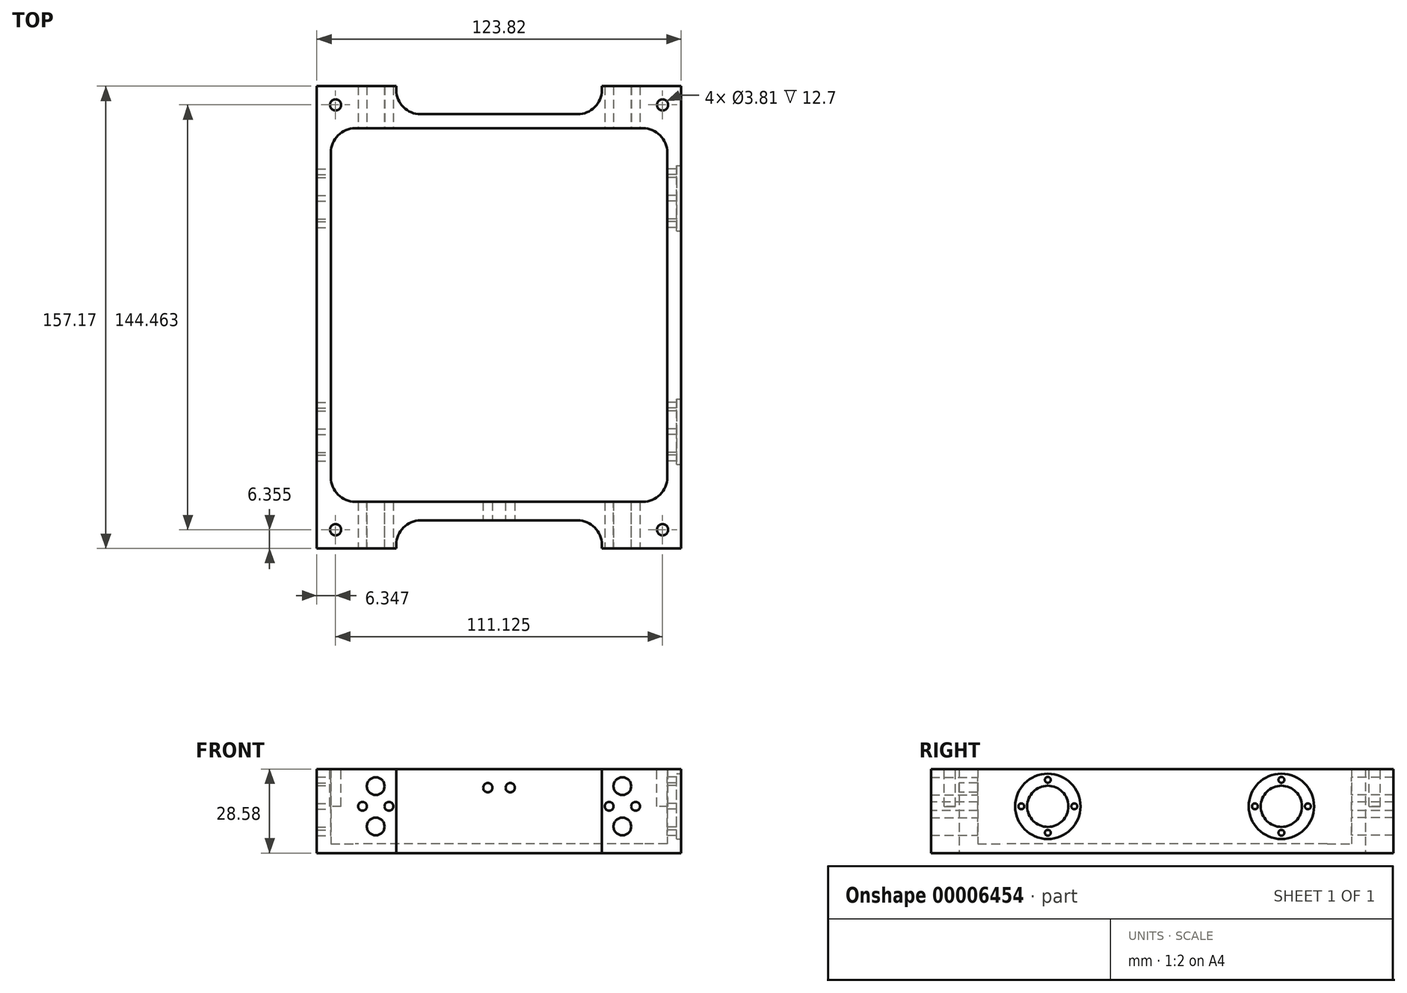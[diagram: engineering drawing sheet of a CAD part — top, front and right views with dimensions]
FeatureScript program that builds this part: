
annotation { "Feature Type Name" : "Feature", "Feature Type Description" : "" }
export const myFeature = defineFeature(function(context is Context, id is Id, definition is map)
    precondition{}
    {
        {
            var Q0;
            Q0=qCreatedBy(makeId("Top.planeOp"),FACE);
            var sketch = newSketch(context, id + "F0", { "sketchPlane" : qUnion([Q0])});
            skLineSegment(sketch, "E0.rect.bottom", {"start": v(48.9, 63.5) * mm, "end": v(-48.9, 63.5) * mm});
            skLineSegment(sketch, "E0.rect.top", {"start": v(48.9, -63.5) * mm, "end": v(-48.9, -63.5) * mm});
            skLineSegment(sketch, "E0.rect.left", {"start": v(57.15, 55.25) * mm, "end": v(57.15, -55.24) * mm});
            skLineSegment(sketch, "E0.rect.right", {"start": v(-57.15, 55.25) * mm, "end": v(-57.15, -55.24) * mm});
            skPoint(sketch, "E0.rect.middle", {"position": v(0, 0) * mm});
            skLineSegment(sketch, "E1.rect.bottom", {"start": v(26.67, 68.26) * mm, "end": v(-26.67, 68.26) * mm});
            skLineSegment(sketch, "E1.rect.top", {"start": v(26.67, -69.85) * mm, "end": v(-26.67, -69.85) * mm});
            skLineSegment(sketch, "E2.top", {"start": v(-61.91, 77.79) * mm, "end": v(-34.93, 77.79) * mm});
            skLineSegment(sketch, "E2.right", {"start": v(-34.93, 76.52) * mm, "end": v(-34.93, 77.79) * mm});
            skLineSegment(sketch, "E3.top", {"start": v(61.91, 77.79) * mm, "end": v(34.92, 77.79) * mm});
            skLineSegment(sketch, "E3.right", {"start": v(34.92, 76.52) * mm, "end": v(34.92, 77.79) * mm});
            skLineSegment(sketch, "E4.top", {"start": v(61.91, -79.37) * mm, "end": v(34.93, -79.37) * mm});
            skLineSegment(sketch, "E4.right", {"start": v(34.93, -78.1) * mm, "end": v(34.93, -79.37) * mm});
            skLineSegment(sketch, "E5.top", {"start": v(-61.91, -79.37) * mm, "end": v(-34.92, -79.37) * mm});
            skLineSegment(sketch, "E5.right", {"start": v(-34.92, -78.1) * mm, "end": v(-34.92, -79.37) * mm});
            skLineSegment(sketch, "E6", {"start": v(-61.91, 77.79) * mm, "end": v(-61.91, -79.37) * mm});
            skLineSegment(sketch, "E7", {"start": v(61.91, -79.37) * mm, "end": v(61.91, 77.79) * mm});
            skLineSegment(sketch, "E8.bottom", {"start": v(-68.26, 71.44) * mm, "end": v(-84.14, 71.44) * mm, "construction": true});
            skLineSegment(sketch, "E8.top", {"start": v(-68.26, 7.94) * mm, "end": v(-84.14, 7.94) * mm, "construction": true});
            skLineSegment(sketch, "E8.left", {"start": v(-68.26, 71.44) * mm, "end": v(-68.26, 7.94) * mm, "construction": true});
            skLineSegment(sketch, "E8.right", {"start": v(-84.14, 71.44) * mm, "end": v(-84.14, 7.94) * mm, "construction": true});
            skLineSegment(sketch, "E9.bottom", {"start": v(-68.26, -71.44) * mm, "end": v(-84.14, -71.44) * mm, "construction": true});
            skLineSegment(sketch, "E9.top", {"start": v(-68.26, -7.94) * mm, "end": v(-84.14, -7.94) * mm, "construction": true});
            skLineSegment(sketch, "E9.left", {"start": v(-68.26, -71.44) * mm, "end": v(-68.26, -7.94) * mm, "construction": true});
            skLineSegment(sketch, "E9.right", {"start": v(-84.14, -71.44) * mm, "end": v(-84.14, -7.94) * mm, "construction": true});
            skLineSegment(sketch, "E10.bottom", {"start": v(87.8, -7) * mm, "end": v(113.59, -7) * mm, "construction": true});
            skLineSegment(sketch, "E10.top", {"start": v(87.8, -69.35) * mm, "end": v(113.59, -69.35) * mm, "construction": true});
            skLineSegment(sketch, "E10.left", {"start": v(87.8, -7) * mm, "end": v(87.8, -69.35) * mm, "construction": true});
            skLineSegment(sketch, "E10.right", {"start": v(113.59, -7) * mm, "end": v(113.59, -69.35) * mm, "construction": true});
            skLineSegment(sketch, "E11.bottom", {"start": v(87.35, 69.72) * mm, "end": v(104.84, 69.72) * mm, "construction": true});
            skLineSegment(sketch, "E11.top", {"start": v(87.35, 26.43) * mm, "end": v(104.84, 26.43) * mm, "construction": true});
            skLineSegment(sketch, "E11.left", {"start": v(87.35, 69.72) * mm, "end": v(87.35, 26.43) * mm, "construction": true});
            skLineSegment(sketch, "E11.right", {"start": v(104.84, 69.72) * mm, "end": v(104.84, 26.43) * mm, "construction": true});
            skLineSegment(sketch, "E12", {"start": v(0, 0) * mm, "end": v(-84.14, 0) * mm, "construction": true});
            skLineSegment(sketch, "E13", {"start": v(-84.14, 7.94) * mm, "end": v(-84.14, 0) * mm, "construction": true});
            skLineSegment(sketch, "E14", {"start": v(-84.14, 0) * mm, "end": v(-84.14, -7.94) * mm, "construction": true});
            skPoint(sketch, "E15.visualSharp", {"position": v(-57.15, 63.5) * mm});
            skArc(sketch, "E15.filletArc", {"start": v(-48.9, 63.5) * mm, "mid": v(-54.73, 61.08) * mm, "end": v(-57.15, 55.25) * mm});
            skPoint(sketch, "E16.visualSharp", {"position": v(57.15, 63.5) * mm});
            skArc(sketch, "E16.filletArc", {"start": v(57.15, 55.25) * mm, "mid": v(54.73, 61.08) * mm, "end": v(48.9, 63.5) * mm});
            skPoint(sketch, "E17.visualSharp", {"position": v(57.15, -63.5) * mm});
            skArc(sketch, "E17.filletArc", {"start": v(48.9, -63.5) * mm, "mid": v(54.73, -61.08) * mm, "end": v(57.15, -55.24) * mm});
            skPoint(sketch, "E18.visualSharp", {"position": v(-57.15, -63.5) * mm});
            skArc(sketch, "E18.filletArc", {"start": v(-57.15, -55.24) * mm, "mid": v(-54.73, -61.08) * mm, "end": v(-48.9, -63.5) * mm});
            skPoint(sketch, "E19.visualSharp", {"position": v(-34.93, 68.26) * mm});
            skArc(sketch, "E19.filletArc", {"start": v(-34.93, 76.52) * mm, "mid": v(-32.5, 70.68) * mm, "end": v(-26.67, 68.26) * mm});
            skPoint(sketch, "E20.visualSharp", {"position": v(34.92, 68.26) * mm});
            skArc(sketch, "E20.filletArc", {"start": v(26.67, 68.26) * mm, "mid": v(32.5, 70.68) * mm, "end": v(34.92, 76.52) * mm});
            skPoint(sketch, "E21.visualSharp", {"position": v(34.93, -69.85) * mm});
            skArc(sketch, "E21.filletArc", {"start": v(34.93, -78.1) * mm, "mid": v(32.5, -72.27) * mm, "end": v(26.67, -69.85) * mm});
            skPoint(sketch, "E22.visualSharp", {"position": v(-34.92, -69.85) * mm});
            skArc(sketch, "E22.filletArc", {"start": v(-26.67, -69.85) * mm, "mid": v(-32.5, -72.27) * mm, "end": v(-34.92, -78.1) * mm});
            skLineSegment(sketch, "E23", {"start": v(-68.26, 39.69) * mm, "end": v(-68.26, -39.69) * mm, "construction": true});
            skSolve(sketch);
        }
        {
            var Q0;
            Q0 = qSketchRegion(id + "F0", true);
            extrude(context, id + "F1", {"entities" : qUnion([Q0]), "depth" : 25.4 * mm});
        }
        {
            var Q0;
            Q0=makeQuery(id+"F1.opExtrude","CAP_FACE",FACE,{"disambiguationData":[OSD([sQuery(id+"F0.wireOp",EDGE,"E0.rect.bottom"),sQuery(id+"F0.wireOp",EDGE,"E0.rect.top"),sQuery(id+"F0.wireOp",EDGE,"E0.rect.left"),sQuery(id+"F0.wireOp",EDGE,"E0.rect.right"),sQuery(id+"F0.wireOp",EDGE,"E1.rect.bottom"),sQuery(id+"F0.wireOp",EDGE,"E1.rect.top"),sQuery(id+"F0.wireOp",EDGE,"E2.top"),sQuery(id+"F0.wireOp",EDGE,"E2.right"),sQuery(id+"F0.wireOp",EDGE,"E3.top"),sQuery(id+"F0.wireOp",EDGE,"E3.right"),sQuery(id+"F0.wireOp",EDGE,"E4.top"),sQuery(id+"F0.wireOp",EDGE,"E4.right"),sQuery(id+"F0.wireOp",EDGE,"E5.top"),sQuery(id+"F0.wireOp",EDGE,"E5.right"),sQuery(id+"F0.wireOp",EDGE,"E6"),sQuery(id+"F0.wireOp",EDGE,"E7"),sQuery(id+"F0.wireOp",EDGE,"E15.filletArc"),sQuery(id+"F0.wireOp",EDGE,"E16.filletArc"),sQuery(id+"F0.wireOp",EDGE,"E17.filletArc"),sQuery(id+"F0.wireOp",EDGE,"E18.filletArc"),sQuery(id+"F0.wireOp",EDGE,"E19.filletArc"),sQuery(id+"F0.wireOp",EDGE,"E20.filletArc"),sQuery(id+"F0.wireOp",EDGE,"E21.filletArc"),sQuery(id+"F0.wireOp",EDGE,"E22.filletArc")])],"isStart":true});
            var sketch = newSketch(context, id + "F2", { "sketchPlane" : qUnion([Q0])});
            skLineSegment(sketch, "E24", {"start": v(-61.91, 79.37) * mm, "end": v(-61.91, -77.79) * mm});
            skLineSegment(sketch, "E25", {"start": v(-61.91, -77.79) * mm, "end": v(-34.93, -77.79) * mm});
            skLineSegment(sketch, "E26", {"start": v(-34.93, -77.79) * mm, "end": v(-34.93, -76.52) * mm});
            skLineSegment(sketch, "E27", {"start": v(34.93, -76.52) * mm, "end": v(34.93, -77.79) * mm});
            skLineSegment(sketch, "E28", {"start": v(34.92, -77.79) * mm, "end": v(61.91, -77.79) * mm});
            skLineSegment(sketch, "E29", {"start": v(61.91, -77.79) * mm, "end": v(61.91, 79.37) * mm});
            skLineSegment(sketch, "E30", {"start": v(61.91, 79.37) * mm, "end": v(34.93, 79.37) * mm});
            skLineSegment(sketch, "E31", {"start": v(34.93, 79.37) * mm, "end": v(34.93, 78.1) * mm});
            skLineSegment(sketch, "E32", {"start": v(26.67, 69.85) * mm, "end": v(-26.67, 69.85) * mm});
            skLineSegment(sketch, "E33", {"start": v(-34.93, 78.1) * mm, "end": v(-34.93, 79.37) * mm});
            skLineSegment(sketch, "E34", {"start": v(-34.92, 79.37) * mm, "end": v(-61.91, 79.37) * mm});
            skLineSegment(sketch, "E35", {"start": v(-26.67, -68.26) * mm, "end": v(26.67, -68.26) * mm});
            skArc(sketch, "E36", {"start": v(-26.67, -68.26) * mm, "mid": v(-32.5, -70.68) * mm, "end": v(-34.92, -76.52) * mm});
            skArc(sketch, "E37", {"start": v(26.67, 69.85) * mm, "mid": v(32.5, 72.27) * mm, "end": v(34.93, 78.1) * mm});
            skArc(sketch, "E38", {"start": v(-34.92, 78.1) * mm, "mid": v(-32.5, 72.27) * mm, "end": v(-26.67, 69.85) * mm});
            skArc(sketch, "E39", {"start": v(34.92, -76.52) * mm, "mid": v(32.5, -70.68) * mm, "end": v(26.67, -68.26) * mm});
            skSolve(sketch);
        }
        {
            var Q0;
            Q0 = qSketchRegion(id + "F2", true);
            extrude(context, id + "F3", {"entities" : qUnion([Q0]), "operationType" : NewBodyOperationType.ADD, "depth" : 3.17 * mm});
        }
        {
            var Q0;
            Q0=makeQuery(id+"F1.opExtrude","SWEPT_FACE",FACE,{"disambiguationData":[OSD([sQuery(id+"F0.wireOp",EDGE,"E0.rect.right")])]});
            var sketch = newSketch(context, id + "F4", { "sketchPlane" : qUnion([Q0])});
            skCircle(sketch, "E40", {"center": v(-39.69, 12.7) * mm, "radius": 7 * mm});
            skCircle(sketch, "E41", {"center": v(39.69, 12.7) * mm, "radius": 7 * mm});
            skCircle(sketch, "E42", {"center": v(-39.69, 12.7) * mm, "radius": 9 * mm, "construction": true});
            skCircle(sketch, "E43", {"center": v(39.69, 12.7) * mm, "radius": 9 * mm, "construction": true});
            skCircle(sketch, "E44", {"center": v(-39.69, 21.7) * mm, "radius": 1 * mm});
            skCircle(sketch, "E45", {"center": v(-30.69, 12.7) * mm, "radius": 1 * mm});
            skCircle(sketch, "E46", {"center": v(-39.69, 3.7) * mm, "radius": 1 * mm});
            skCircle(sketch, "E47", {"center": v(-48.69, 12.7) * mm, "radius": 1 * mm});
            skCircle(sketch, "E48", {"center": v(30.69, 12.7) * mm, "radius": 1 * mm});
            skCircle(sketch, "E49", {"center": v(39.69, 21.7) * mm, "radius": 1 * mm});
            skCircle(sketch, "E50", {"center": v(48.69, 12.7) * mm, "radius": 1 * mm});
            skCircle(sketch, "E51", {"center": v(39.69, 3.7) * mm, "radius": 1 * mm});
            skLineSegment(sketch, "E52", {"start": v(-39.69, 12.7) * mm, "end": v(0, 25.4) * mm, "construction": true});
            skLineSegment(sketch, "E53", {"start": v(0, 25.4) * mm, "end": v(39.69, 12.7) * mm, "construction": true});
            skLineSegment(sketch, "E54", {"start": v(-39.69, 12.7) * mm, "end": v(-39.69, 25.4) * mm, "construction": true});
            skLineSegment(sketch, "E55", {"start": v(-39.69, 12.7) * mm, "end": v(-39.69, 0) * mm, "construction": true});
            skSolve(sketch);
        }
        {
            var Q0;
            Q0 = qSketchRegion(id + "F4", true);
            extrude(context, id + "F5", {"entities" : qUnion([Q0]), "operationType" : NewBodyOperationType.REMOVE, "endBound" : BoundingType.THROUGH_ALL, "oppositeDirection" : true, "depth" : 25.4 * mm});
        }
        {
            var Q0;
            Q0 = qSketchRegion(id + "F4", true);
            extrude(context, id + "F6", {"entities" : qUnion([Q0]), "operationType" : NewBodyOperationType.REMOVE, "endBound" : BoundingType.THROUGH_ALL, "depth" : 25.4 * mm});
        }
        {
            var Q0;
            Q0=makeQuery(id+"F1.opExtrude","CAP_FACE",FACE,{"disambiguationData":[OSD([sQuery(id+"F0.wireOp",EDGE,"E0.rect.bottom"),sQuery(id+"F0.wireOp",EDGE,"E0.rect.top"),sQuery(id+"F0.wireOp",EDGE,"E0.rect.left"),sQuery(id+"F0.wireOp",EDGE,"E0.rect.right"),sQuery(id+"F0.wireOp",EDGE,"E1.rect.bottom"),sQuery(id+"F0.wireOp",EDGE,"E1.rect.top"),sQuery(id+"F0.wireOp",EDGE,"E2.top"),sQuery(id+"F0.wireOp",EDGE,"E2.right"),sQuery(id+"F0.wireOp",EDGE,"E3.top"),sQuery(id+"F0.wireOp",EDGE,"E3.right"),sQuery(id+"F0.wireOp",EDGE,"E4.top"),sQuery(id+"F0.wireOp",EDGE,"E4.right"),sQuery(id+"F0.wireOp",EDGE,"E5.top"),sQuery(id+"F0.wireOp",EDGE,"E5.right"),sQuery(id+"F0.wireOp",EDGE,"E6"),sQuery(id+"F0.wireOp",EDGE,"E7"),sQuery(id+"F0.wireOp",EDGE,"E15.filletArc"),sQuery(id+"F0.wireOp",EDGE,"E16.filletArc"),sQuery(id+"F0.wireOp",EDGE,"E17.filletArc"),sQuery(id+"F0.wireOp",EDGE,"E18.filletArc"),sQuery(id+"F0.wireOp",EDGE,"E19.filletArc"),sQuery(id+"F0.wireOp",EDGE,"E20.filletArc"),sQuery(id+"F0.wireOp",EDGE,"E21.filletArc"),sQuery(id+"F0.wireOp",EDGE,"E22.filletArc")])],"isStart":false});
            var sketch = newSketch(context, id + "F7", { "sketchPlane" : qUnion([Q0])});
            skLineSegment(sketch, "E56.bottom", {"start": v(-55.56, 71.44) * mm, "end": v(55.56, 71.44) * mm, "construction": true});
            skLineSegment(sketch, "E56.top", {"start": v(-55.56, -73.02) * mm, "end": v(55.56, -73.02) * mm, "construction": true});
            skLineSegment(sketch, "E56.left", {"start": v(-55.56, 71.44) * mm, "end": v(-55.56, -73.02) * mm, "construction": true});
            skLineSegment(sketch, "E56.right", {"start": v(55.56, 71.44) * mm, "end": v(55.56, -73.02) * mm, "construction": true});
            skCircle(sketch, "E57", {"center": v(-55.56, 71.44) * mm, "radius": 1.9 * mm});
            skCircle(sketch, "E58", {"center": v(55.56, 71.44) * mm, "radius": 1.9 * mm});
            skCircle(sketch, "E59", {"center": v(55.56, -73.02) * mm, "radius": 1.9 * mm});
            skCircle(sketch, "E60", {"center": v(-55.56, -73.02) * mm, "radius": 1.9 * mm});
            skSolve(sketch);
        }
        {
            var Q0;
            Q0 = qSketchRegion(id + "F7", true);
            extrude(context, id + "F8", {"entities" : qUnion([Q0]), "operationType" : NewBodyOperationType.REMOVE, "oppositeDirection" : true, "depth" : 12.7 * mm});
        }
        {
            var Q0;
            Q0=makeQuery(id+"F3.boolean.opBoolean","MERGE",FACE,{"derivedFrom":[makeQuery(id+"F1.opExtrude","SWEPT_FACE",FACE,{"disambiguationData":[OSD([sQuery(id+"F0.wireOp",EDGE,"E1.rect.top")])]}),makeQuery(id+"F3.opExtrude","SWEPT_FACE",FACE,{"disambiguationData":[OSD([sQuery(id+"F2.wireOp",EDGE,"E32")])]})]});
            var sketch = newSketch(context, id + "F9", { "sketchPlane" : qUnion([Q0])});
            skLineSegment(sketch, "E61.bottom", {"start": v(-6.35, 25.4) * mm, "end": v(6.35, 25.4) * mm, "construction": true});
            skLineSegment(sketch, "E61.top", {"start": v(-6.35, 12.7) * mm, "end": v(6.35, 12.7) * mm, "construction": true});
            skLineSegment(sketch, "E61.left", {"start": v(-6.35, 25.4) * mm, "end": v(-6.35, 12.7) * mm, "construction": true});
            skLineSegment(sketch, "E61.right", {"start": v(6.35, 25.4) * mm, "end": v(6.35, 12.7) * mm, "construction": true});
            skLineSegment(sketch, "E62", {"start": v(-6.35, 25.4) * mm, "end": v(-26.67, 25.4) * mm, "construction": true});
            skLineSegment(sketch, "E63", {"start": v(-26.67, 25.4) * mm, "end": v(-6.35, 25.4) * mm, "construction": true});
            skLineSegment(sketch, "E64", {"start": v(6.35, 25.4) * mm, "end": v(26.67, 25.4) * mm, "construction": true});
            skLineSegment(sketch, "E65", {"start": v(-6.35, 12.7) * mm, "end": v(-26.67, 25.4) * mm, "construction": true});
            skLineSegment(sketch, "E66", {"start": v(6.35, 12.7) * mm, "end": v(26.67, 25.4) * mm, "construction": true});
            skLineSegment(sketch, "E67", {"start": v(-6.35, 19.05) * mm, "end": v(-3.8, 19.05) * mm, "construction": true});
            skLineSegment(sketch, "E68", {"start": v(0, 25.4) * mm, "end": v(4.67, 25.4) * mm, "construction": true});
            skLineSegment(sketch, "E69", {"start": v(6.35, 19.05) * mm, "end": v(3.81, 19.05) * mm, "construction": true});
            skCircle(sketch, "E70", {"center": v(-3.8, 19.05) * mm, "radius": 1.59 * mm});
            skCircle(sketch, "E71", {"center": v(3.81, 19.05) * mm, "radius": 1.59 * mm});
            skSolve(sketch);
        }
        {
            var Q0;
            Q0 = qSketchRegion(id + "F9", true);
            extrude(context, id + "F10", {"entities" : qUnion([Q0]), "operationType" : NewBodyOperationType.REMOVE, "endBound" : BoundingType.UP_TO_NEXT, "oppositeDirection" : true, "depth" : 25.4 * mm});
        }
        {
            var Q0;
            Q0=makeQuery(id+"F1.opExtrude","SWEPT_FACE",FACE,{"disambiguationData":[OSD([sQuery(id+"F0.wireOp",EDGE,"E0.rect.bottom")])]});
            var sketch = newSketch(context, id + "F11", { "sketchPlane" : qUnion([Q0])});
            skCircle(sketch, "E72", {"center": v(-41.91, 19.56) * mm, "radius": 3 * mm});
            skCircle(sketch, "E73", {"center": v(-41.91, 5.84) * mm, "radius": 3 * mm});
            skCircle(sketch, "E74", {"center": v(41.91, 19.56) * mm, "radius": 3 * mm});
            skCircle(sketch, "E75", {"center": v(41.91, 5.84) * mm, "radius": 3 * mm});
            skLineSegment(sketch, "E76.bottom", {"start": v(-41.91, 19.56) * mm, "end": v(41.91, 19.56) * mm, "construction": true});
            skLineSegment(sketch, "E76.top", {"start": v(-41.91, 5.84) * mm, "end": v(41.91, 5.84) * mm, "construction": true});
            skLineSegment(sketch, "E76.left", {"start": v(-41.91, 19.56) * mm, "end": v(-41.91, 5.84) * mm, "construction": true});
            skLineSegment(sketch, "E76.right", {"start": v(41.91, 19.56) * mm, "end": v(41.91, 5.84) * mm, "construction": true});
            skSolve(sketch);
        }
        {
            var Q0;
            Q0 = qSketchRegion(id + "F11", true);
            extrude(context, id + "F12", {"entities" : qUnion([Q0]), "operationType" : NewBodyOperationType.REMOVE, "endBound" : BoundingType.THROUGH_ALL, "oppositeDirection" : true, "depth" : 25.4 * mm});
        }
        {
            var Q0;
            Q0 = qSketchRegion(id + "F11", true);
            extrude(context, id + "F13", {"entities" : qUnion([Q0]), "operationType" : NewBodyOperationType.REMOVE, "endBound" : BoundingType.THROUGH_ALL, "depth" : 25.4 * mm});
        }
        {
            var Q0;
            Q0=makeQuery(id+"F3.boolean.opBoolean","MERGE",FACE,{"derivedFrom":[makeQuery(id+"F1.opExtrude","SWEPT_FACE",FACE,{"disambiguationData":[OSD([sQuery(id+"F0.wireOp",EDGE,"E5.top")])]}),makeQuery(id+"F3.opExtrude","SWEPT_FACE",FACE,{"disambiguationData":[OSD([sQuery(id+"F2.wireOp",EDGE,"E34")])]})]});
            var sketch = newSketch(context, id + "F14", { "sketchPlane" : qUnion([Q0])});
            skLineSegment(sketch, "E77.bottom", {"start": v(-41.91, 19.56) * mm, "end": v(41.91, 19.56) * mm});
            skLineSegment(sketch, "E77.top", {"start": v(-41.91, 5.84) * mm, "end": v(41.91, 5.84) * mm});
            skLineSegment(sketch, "E77.left", {"start": v(-41.91, 19.56) * mm, "end": v(-41.91, 5.84) * mm});
            skLineSegment(sketch, "E77.right", {"start": v(41.91, 19.56) * mm, "end": v(41.91, 5.84) * mm});
            skSolve(sketch);
        }
        {
            var Q0;
            Q0=makeQuery(id+"F3.boolean.opBoolean","MERGE",FACE,{"derivedFrom":[makeQuery(id+"F1.opExtrude","SWEPT_FACE",FACE,{"disambiguationData":[OSD([sQuery(id+"F0.wireOp",EDGE,"E7")])]}),makeQuery(id+"F3.opExtrude","SWEPT_FACE",FACE,{"disambiguationData":[OSD([sQuery(id+"F2.wireOp",EDGE,"E29")])]})]});
            var sketch = newSketch(context, id + "F15", { "sketchPlane" : qUnion([Q0])});
            skCircle(sketch, "E78", {"center": v(-39.69, 12.7) * mm, "radius": 11.11 * mm});
            skCircle(sketch, "E79", {"center": v(-39.69, 21.7) * mm, "radius": 2 * mm, "construction": true});
            skCircle(sketch, "E80", {"center": v(39.69, 12.7) * mm, "radius": 11.11 * mm});
            skSolve(sketch);
        }
        {
            var Q0;
            Q0 = qSketchRegion(id + "F15", true);
            extrude(context, id + "F16", {"entities" : qUnion([Q0]), "operationType" : NewBodyOperationType.REMOVE, "oppositeDirection" : true, "depth" : 1.59 * mm});
        }
        {
            var Q0;
            {var subQ0=sQuery(id+"F0.wireOp",EDGE,"E5.top");var subQ13=makeQuery(id+"F1.opExtrude","CAP_EDGE",EDGE,{"disambiguationData":[OSD([subQ0])],"isStart":false});Q0=makeQuery(id+"F14.imprint","IMPRINT",FACE,{"disambiguationData":[TD([[makeQuery(id+"F14.imprint","IMPRINT",EDGE,{"derivedFrom":subQ13}),-1.0]])]});}
            var sketch = newSketch(context, id + "F17", { "sketchPlane" : qUnion([Q0])});
            skCircle(sketch, "E81", {"center": v(-46.4, 12.7) * mm, "radius": 1.5 * mm});
            skCircle(sketch, "E82", {"center": v(-37.43, 12.7) * mm, "radius": 1.5 * mm});
            skCircle(sketch, "E83", {"center": v(37.43, 12.7) * mm, "radius": 1.5 * mm});
            skCircle(sketch, "E84", {"center": v(46.4, 12.7) * mm, "radius": 1.5 * mm});
            skLineSegment(sketch, "E85", {"start": v(-46.4, 12.7) * mm, "end": v(-37.43, 12.7) * mm, "construction": true});
            skLineSegment(sketch, "E86", {"start": v(37.43, 12.7) * mm, "end": v(46.4, 12.7) * mm, "construction": true});
            skLineSegment(sketch, "E87", {"start": v(-37.43, 12.7) * mm, "end": v(37.43, 12.7) * mm, "construction": true});
            skSolve(sketch);
        }
        {
            var Q0;
            Q0 = qSketchRegion(id + "F17", true);
            extrude(context, id + "F18", {"entities" : qUnion([Q0]), "operationType" : NewBodyOperationType.REMOVE, "endBound" : BoundingType.THROUGH_ALL, "oppositeDirection" : true, "depth" : 25.4 * mm});
        }
    });
